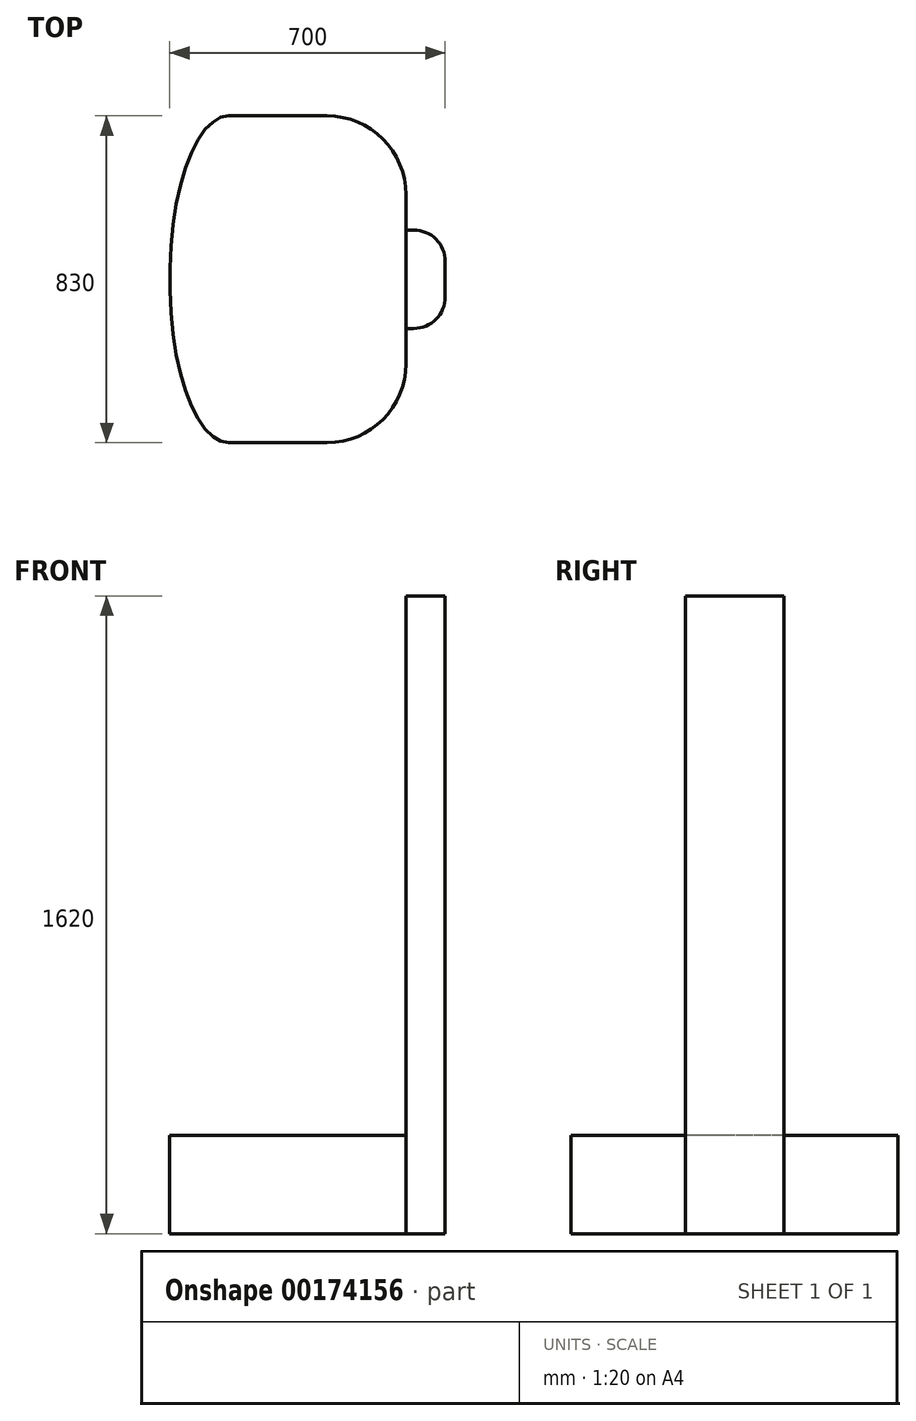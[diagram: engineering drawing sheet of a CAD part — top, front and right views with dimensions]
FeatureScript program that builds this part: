
annotation { "Feature Type Name" : "Feature", "Feature Type Description" : "" }
export const myFeature = defineFeature(function(context is Context, id is Id, definition is map)
    precondition{}
    {
        {
            var Q0;
            Q0=qCreatedBy(makeId("Top.planeOp"),FACE);
            var sketch = newSketch(context, id + "F0", { "sketchPlane" : qUnion([Q0])});
            skLineSegment(sketch, "E0", {"start": v(-450, 415) * mm, "end": v(-200, 415) * mm});
            skLineSegment(sketch, "E1", {"start": v(0, 215) * mm, "end": v(0, -215) * mm});
            skLineSegment(sketch, "E2", {"start": v(-200, -415) * mm, "end": v(-450, -415) * mm});
            skEllipticalArc(sketch, "E3", {});
            skArc(sketch, "E4.filletArc", {"start": v(0, 215) * mm, "mid": v(-58.58, 356.42) * mm, "end": v(-200, 415) * mm});
            skArc(sketch, "E5.filletArc", {"start": v(-200, -415) * mm, "mid": v(-58.58, -356.42) * mm, "end": v(0, -215) * mm});
            skLineSegment(sketch, "E6", {"start": v(-450, 0) * mm, "end": v(-600, 0) * mm, "construction": true});
            const initialGuessF0  = {"E3": [-0.45, 0, 0, 1, 0.415, 0.15, 0, 3.141592653589793]};
            skSetInitialGuess(sketch, initialGuessF0);
            skSolve(sketch);
        }
        {
            var Q0;
            Q0=makeQuery(id+"F0.imprint","IMPRINT",FACE,{"disambiguationData":[TD([[makeQuery(id+"F0.imprint","IMPRINT",EDGE,{"derivedFrom":sQuery(id+"F0.wireOp",EDGE,"E0")}),-1.0]])]});
            extrude(context, id + "F1", {"entities" : qUnion([Q0]), "depth" : 250 * mm});
        }
        {
            var Q0;
            Q0=qCreatedBy(makeId("Top.planeOp"),FACE);
            var sketch = newSketch(context, id + "F2", { "sketchPlane" : qUnion([Q0])});
            skLineSegment(sketch, "E7.bottom", {"start": v(0, 125) * mm, "end": v(20, 125) * mm});
            skLineSegment(sketch, "E7.top", {"start": v(0, -125) * mm, "end": v(20, -125) * mm});
            skLineSegment(sketch, "E7.left", {"start": v(0, 125) * mm, "end": v(0, -125) * mm});
            skLineSegment(sketch, "E7.right", {"start": v(100, 45) * mm, "end": v(100, -45) * mm});
            skPoint(sketch, "E8.visualSharp", {"position": v(100, 125) * mm});
            skArc(sketch, "E8.filletArc", {"start": v(100, 45) * mm, "mid": v(76.57, 101.57) * mm, "end": v(20, 125) * mm});
            skPoint(sketch, "E9.visualSharp", {"position": v(100, -125) * mm});
            skArc(sketch, "E9.filletArc", {"start": v(20, -125) * mm, "mid": v(76.57, -101.57) * mm, "end": v(100, -45) * mm});
            skSolve(sketch);
        }
        {
            var Q0;
            Q0=makeQuery(id+"F2.imprint","IMPRINT",FACE,{"disambiguationData":[TD([[makeQuery(id+"F2.imprint","IMPRINT",EDGE,{"derivedFrom":sQuery(id+"F2.wireOp",EDGE,"E7.bottom")}),-1.0]])]});
            extrude(context, id + "F3", {"entities" : qUnion([Q0]), "operationType" : NewBodyOperationType.ADD, "depth" : 1620 * mm});
        }
    });
